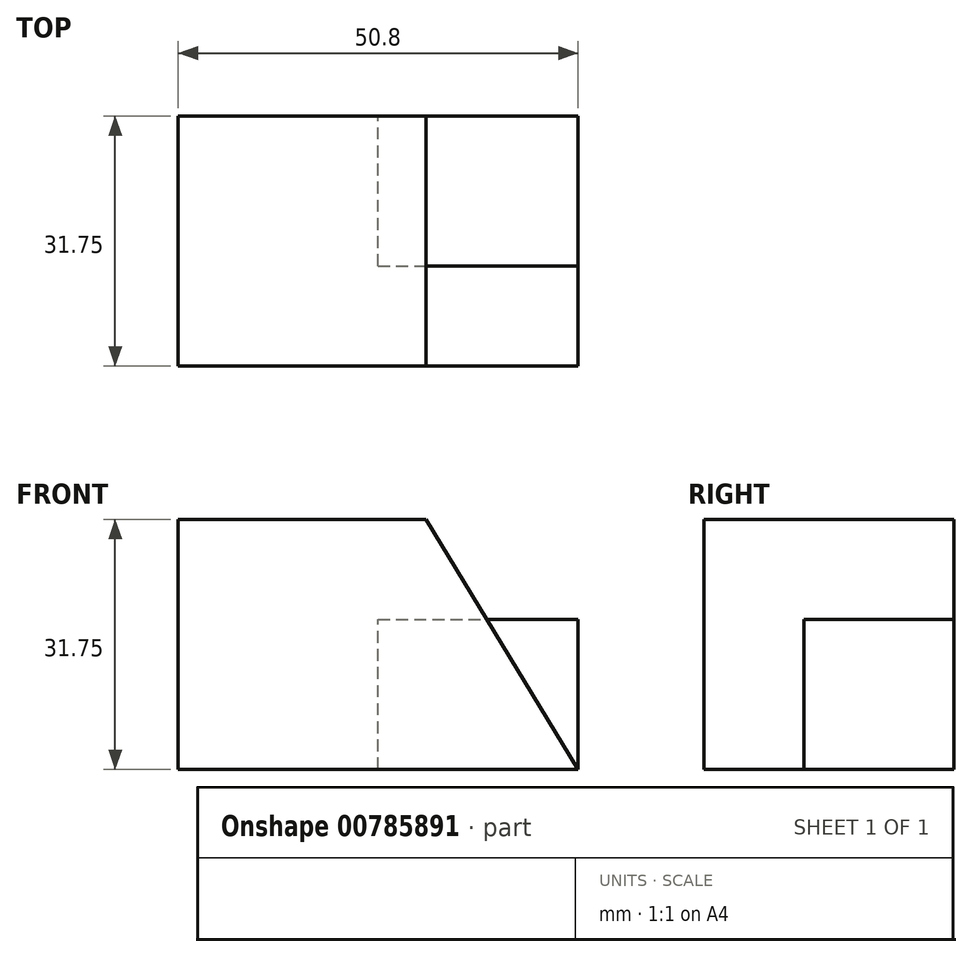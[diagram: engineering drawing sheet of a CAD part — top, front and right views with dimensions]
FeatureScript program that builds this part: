
annotation { "Feature Type Name" : "Feature", "Feature Type Description" : "" }
export const myFeature = defineFeature(function(context is Context, id is Id, definition is map)
    precondition{}
    {
        {
            var Q0;
            Q0=qCreatedBy(makeId("Front.planeOp"),FACE);
            var sketch = newSketch(context, id + "F0", { "sketchPlane" : qUnion([Q0])});
            skLineSegment(sketch, "E0", {"start": v(0, 0) * mm, "end": v(50.8, 0) * mm});
            skLineSegment(sketch, "E1", {"start": v(50.8, 0) * mm, "end": v(50.8, 31.75) * mm});
            skLineSegment(sketch, "E2", {"start": v(50.8, 31.75) * mm, "end": v(0, 31.75) * mm});
            skLineSegment(sketch, "E3", {"start": v(0, 31.75) * mm, "end": v(0, 0) * mm});
            skSolve(sketch);
        }
        {
            var Q0;
            Q0 = qSketchRegion(id + "F0", true);
            extrude(context, id + "F1", {"entities" : qUnion([Q0]), "depth" : 31.75 * mm, "offsetDistance" : 25.4 * mm});
        }
        {
            var Q0;
            Q0=makeQuery(id+"F1.opExtrude","SWEPT_FACE",FACE,{"disambiguationData":[OSD([sQuery(id+"F0.wireOp",EDGE,"E1")])]});
            var sketch = newSketch(context, id + "F2", { "sketchPlane" : qUnion([Q0])});
            skLineSegment(sketch, "E4", {"start": v(-31.75, 0) * mm, "end": v(-19.05, 0) * mm});
            skLineSegment(sketch, "E5", {"start": v(-19.05, 0) * mm, "end": v(-19.05, 19.05) * mm});
            skLineSegment(sketch, "E6", {"start": v(-19.05, 19.05) * mm, "end": v(0, 19.05) * mm});
            skLineSegment(sketch, "E7", {"start": v(0, 19.05) * mm, "end": v(0, 31.75) * mm});
            skLineSegment(sketch, "E8", {"start": v(0, 31.75) * mm, "end": v(-31.75, 31.75) * mm});
            skLineSegment(sketch, "E9", {"start": v(-31.75, 31.75) * mm, "end": v(-31.75, 0) * mm});
            skSolve(sketch);
        }
        {
            var Q0;
            Q0=makeQuery(id+"F1.opExtrude","CAP_FACE",FACE,{"disambiguationData":[OSD([sQuery(id+"F0.wireOp",EDGE,"E0"),sQuery(id+"F0.wireOp",EDGE,"E1"),sQuery(id+"F0.wireOp",EDGE,"E2"),sQuery(id+"F0.wireOp",EDGE,"E3")])],"isStart":false});
            var sketch = newSketch(context, id + "F3", { "sketchPlane" : qUnion([Q0])});
            skLineSegment(sketch, "E10", {"start": v(50.8, 0) * mm, "end": v(31.47, 31.75) * mm});
            skLineSegment(sketch, "E11", {"start": v(31.47, 31.75) * mm, "end": v(50.8, 31.75) * mm});
            skLineSegment(sketch, "E12", {"start": v(50.8, 31.75) * mm, "end": v(50.8, 0) * mm});
            skSolve(sketch);
        }
        {
            var Q0;
            Q0 = qSketchRegion(id + "F3", true);
            extrude(context, id + "F4", {"entities" : qUnion([Q0]), "operationType" : NewBodyOperationType.REMOVE, "oppositeDirection" : true, "depth" : 31.75 * mm, "offsetDistance" : 25.4 * mm});
        }
        {
            var Q0;
            {var subQ0=sQuery(id+"F2.wireOp",EDGE,"E5");Q0=makeQuery(id+"F2.imprint","IMPRINT",FACE,{"disambiguationData":[TD([[makeQuery(id+"F2.imprint","IMPRINT",EDGE,{"derivedFrom":subQ0}),-1.0]])]});}
            extrude(context, id + "F5", {"entities" : qUnion([Q0]), "oppositeDirection" : true, "depth" : 25.4 * mm, "offsetDistance" : 25.4 * mm});
        }
    });
